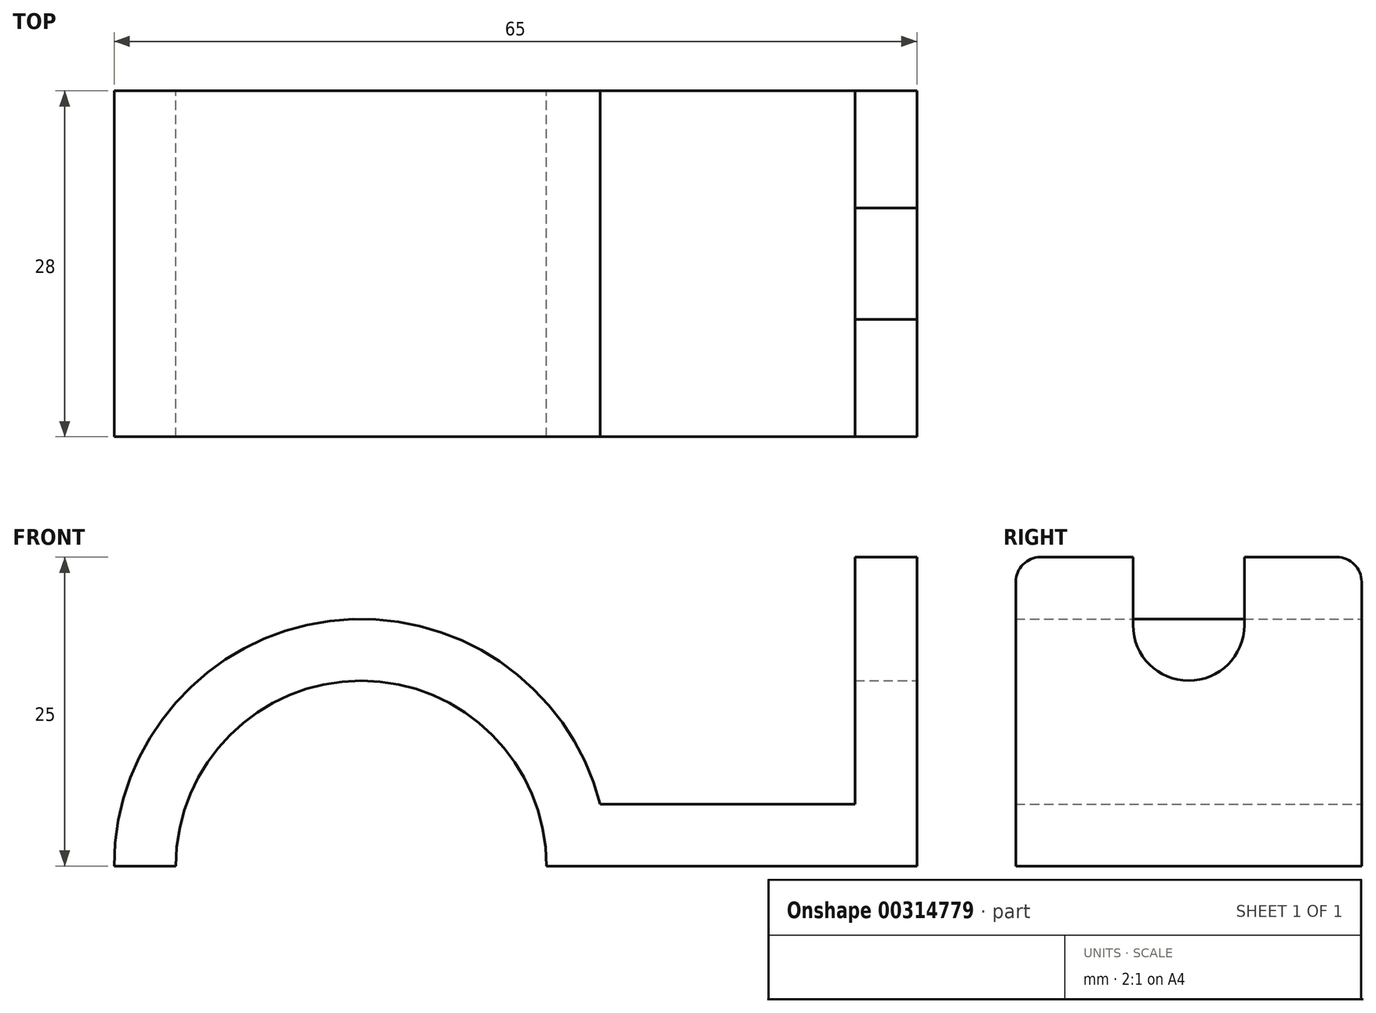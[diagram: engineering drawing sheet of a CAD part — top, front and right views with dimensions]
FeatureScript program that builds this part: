
annotation { "Feature Type Name" : "Feature", "Feature Type Description" : "" }
export const myFeature = defineFeature(function(context is Context, id is Id, definition is map)
    precondition{}
    {
        {
            var Q0;
            Q0=qCreatedBy(makeId("Front.planeOp"),FACE);
            var sketch = newSketch(context, id + "F0", { "sketchPlane" : qUnion([Q0])});
            skLineSegment(sketch, "E0", {"start": v(-25.93, 0) * mm, "end": v(34.74, 0) * mm, "construction": true});
            skLineSegment(sketch, "E1", {"start": v(0, 0) * mm, "end": v(0, 30.84) * mm, "construction": true});
            skArc(sketch, "E2", {"start": v(15, 0) * mm, "mid": v(0, 15) * mm, "end": v(-15, 0) * mm});
            skArc(sketch, "E3", {"start": v(19.36, 5) * mm, "mid": v(-2.52, 19.84) * mm, "end": v(-20, 0) * mm});
            skLineSegment(sketch, "E4", {"start": v(15, 0) * mm, "end": v(45, 0) * mm});
            skLineSegment(sketch, "E5", {"start": v(45, 0) * mm, "end": v(45, 25) * mm});
            skLineSegment(sketch, "E6", {"start": v(45, 25) * mm, "end": v(40, 25) * mm});
            skLineSegment(sketch, "E7", {"start": v(40, 25) * mm, "end": v(40, 5) * mm});
            skLineSegment(sketch, "E8", {"start": v(40, 5) * mm, "end": v(19.36, 5) * mm});
            skLineSegment(sketch, "E9", {"start": v(-15, 0) * mm, "end": v(-20, 0) * mm});
            skSolve(sketch);
        }
        {
            var Q0;
            Q0 = qSketchRegion(id + "F0", true);
            extrude(context, id + "F1", {"entities" : qUnion([Q0]), "depth" : 28 * mm, "symmetric" : true});
        }
        {
            var Q0;
            Q0=makeQuery(id+"F1.opExtrude","SWEPT_FACE",FACE,{"disambiguationData":[OSD([sQuery(id+"F0.wireOp",EDGE,"E5")])]});
            var sketch = newSketch(context, id + "F2", { "sketchPlane" : qUnion([Q0])});
            skLineSegment(sketch, "E10", {"start": v(0, 25) * mm, "end": v(0, 19.5) * mm, "construction": true});
            skPoint(sketch, "E10.endSnap0", {"position": v(0, 25) * mm});
            skLineSegment(sketch, "E11", {"start": v(-14, 15) * mm, "end": v(14, 15) * mm});
            skArc(sketch, "E12", {"start": v(-4.5, 19.5) * mm, "mid": v(0, 15) * mm, "end": v(4.5, 19.5) * mm});
            skLineSegment(sketch, "E13", {"start": v(4.5, 19.5) * mm, "end": v(4.5, 25) * mm});
            skLineSegment(sketch, "E14", {"start": v(-4.5, 19.5) * mm, "end": v(-4.5, 25) * mm});
            skSolve(sketch);
        }
        {
            var Q0;
            {var subQ1=sQuery(id+"F2.wireOp",EDGE,"E13");Q0=makeQuery(id+"F2.imprint","IMPRINT",FACE,{"disambiguationData":[TD([[makeQuery(id+"F2.imprint","IMPRINT",EDGE,{"derivedFrom":subQ1}),1.0]])]});}
            var Q1;
            Q1=makeQuery(id+"F1.opExtrude","CAP_VERTEX",VERTEX,{"disambiguationData":[OSD([sQuery(id+"F0.wireOp",EDGE,"E6"),sQuery(id+"F0.wireOp",EDGE,"E7")])],"isStart":true});
            extrude(context, id + "F3", {"entities" : qUnion([Q0]), "operationType" : NewBodyOperationType.REMOVE, "endBound" : BoundingType.UP_TO_VERTEX, "oppositeDirection" : true, "endBoundEntityVertex" : qUnion([Q1]), "depth" : 25 * mm});
        }
        {
            var Q0;
            Q0=makeQuery(id+"F1.opExtrude","CAP_EDGE",EDGE,{"disambiguationData":[OSD([sQuery(id+"F0.wireOp",EDGE,"E6")])],"isStart":false});
            var Q1;
            Q1=makeQuery(id+"F1.opExtrude","CAP_EDGE",EDGE,{"disambiguationData":[OSD([sQuery(id+"F0.wireOp",EDGE,"E6")])],"isStart":true});
            fillet(context, id + "F4", {"entities" : qUnion([Q0, Q1]), "radius" : 2 * mm, "tangentPropagation" : true, "allowEdgeOverflow" : false});
        }
    });
